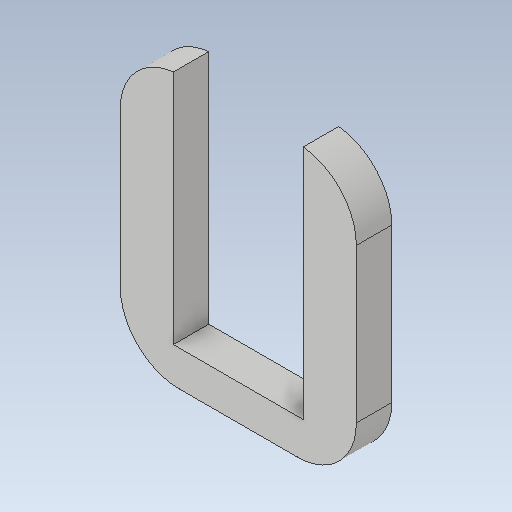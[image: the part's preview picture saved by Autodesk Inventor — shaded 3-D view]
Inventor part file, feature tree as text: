
AUTODESK INVENTOR PART (.ipt)
format: ipt  version: 2020 (Build 240168000, 168)  size: 116,224 bytes
history: native  units: in
note: dims shown in document units (in); Inventor stores cm internally (conversion verified against a paired STEP export)
features: other x1, extrude x1, fillet x1, sketch x1
ambient origin geometry x8: Origin, YZ Plane, XZ Plane, XY Plane, X Axis, Y Axis, Z Axis, Center Point
bodies: Body1 (feature_tree)
feature tree (4):
  other  "Sólido1"
  extrude  "Extrusión1"  Depth=0.7874in
  fillet  "Empalme1"  Radius=0.4331in
  sketch  "Boceto1"  dims[d0=0.7874in d1=0.7874in d2=0.4331in d4=0.2756in d5=0.1181in d6=0.9055in d7=0.1181in d8=0.0in d9=0.1969in]
